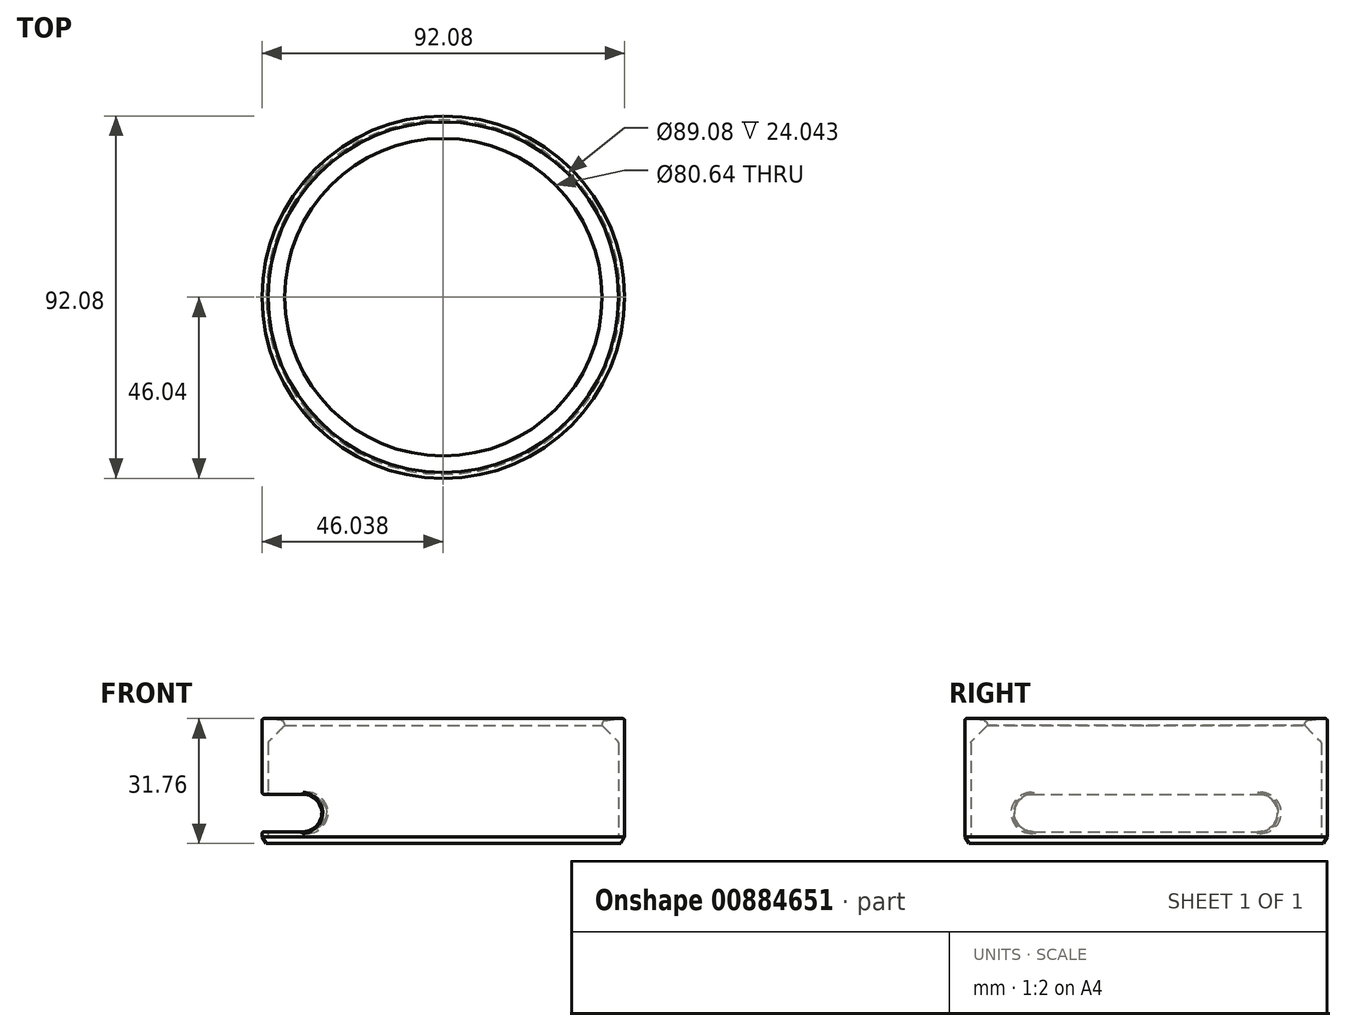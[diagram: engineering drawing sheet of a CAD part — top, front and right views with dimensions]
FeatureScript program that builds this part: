
annotation { "Feature Type Name" : "Feature", "Feature Type Description" : "" }
export const myFeature = defineFeature(function(context is Context, id is Id, definition is map)
    precondition{}
    {
        {
            var Q0;
            Q0=qCreatedBy(makeId("Front.planeOp"),FACE);
            var sketch = newSketch(context, id + "F0", { "sketchPlane" : qUnion([Q0])});
            skLineSegment(sketch, "E0.bottom", {"start": v(0.75, 15.88) * mm, "end": v(-0.75, 15.88) * mm});
            skLineSegment(sketch, "E0.right", {"start": v(-0.75, 15.88) * mm, "end": v(-0.75, -15.88) * mm});
            skPoint(sketch, "E0.middle", {"position": v(0, 0) * mm});
            skLineSegment(sketch, "E1.bottom", {"start": v(-0.75, -15.88) * mm, "end": v(45.29, -15.88) * mm});
            skLineSegment(sketch, "E1.top", {"start": v(0.75, -14.37) * mm, "end": v(45.29, -14.37) * mm});
            skLineSegment(sketch, "E1.right", {"start": v(45.29, -15.87) * mm, "end": v(45.29, -14.37) * mm});
            skLineSegment(sketch, "E2", {"start": v(0.75, 15.88) * mm, "end": v(4.97, 15.24) * mm});
            skLineSegment(sketch, "E3", {"start": v(4.97, 14.1) * mm, "end": v(0.75, 9.87) * mm});
            skLineSegment(sketch, "E4.trimOffspring", {"start": v(0.75, 9.88) * mm, "end": v(0.75, -14.38) * mm});
            skLineSegment(sketch, "E5", {"start": v(0.75, 15.88) * mm, "end": v(0.75, 9.88) * mm, "construction": true});
            skLineSegment(sketch, "E6", {"start": v(4.97, 14.1) * mm, "end": v(4.97, 15.24) * mm});
            skPoint(sketch, "E7.orphan", {"position": v(0.75, -15.88) * mm});
            skLineSegment(sketch, "E8", {"start": v(4.97, 14.66) * mm, "end": v(0.75, 14.66) * mm, "construction": true});
            skSolve(sketch);
        }
        {
            var Q0;
            Q0=makeQuery(id+"F0.imprint","IMPRINT",FACE,{"disambiguationData":[TD([[makeQuery(id+"F0.imprint","IMPRINT",EDGE,{"derivedFrom":sQuery(id+"F0.wireOp",EDGE,"E0.bottom")}),1.0]])]});
            var Q1;
            Q1=sQuery(id+"F0.wireOp",EDGE,"E1.right");
            revolve(context, id + "F1", {"surfaceOperationType" : NewSurfaceOperationType.NEW, "entities" : qUnion([Q0]), "axis" : qUnion([Q1]), "revolveType" : RevolveType.FULL});
        }
        {
            var Q0;
            Q0=qCreatedBy(makeId("Right.planeOp"),FACE);
            var sketch = newSketch(context, id + "F2", { "sketchPlane" : qUnion([Q0])});
            skLineSegment(sketch, "E9.bottom", {"start": v(28.57, -12.88) * mm, "end": v(-28.57, -12.88) * mm});
            skLineSegment(sketch, "E9.top", {"start": v(28.8, -3.35) * mm, "end": v(-28.8, -3.35) * mm});
            skPoint(sketch, "E9.middle", {"position": v(0, 0) * mm});
            skArc(sketch, "E10", {"start": v(28.57, -12.88) * mm, "mid": v(33.45, -8.22) * mm, "end": v(28.8, -3.35) * mm});
            skArc(sketch, "E11.MirrorC", {"start": v(-28.57, -12.88) * mm, "mid": v(-33.45, -8.22) * mm, "end": v(-28.8, -3.35) * mm});
            skPoint(sketch, "E12", {"position": v(33.45, -8.22) * mm});
            skPoint(sketch, "E13", {"position": v(-33.45, -8.22) * mm});
            skLineSegment(sketch, "E14.0", {"start": v(46.04, -15.88) * mm, "end": v(-46.04, -15.88) * mm, "construction": true});
            skSolve(sketch);
        }
        {
            var Q0;
            Q0 = qSketchRegion(id + "F2", true);
            extrude(context, id + "F3", {"entities" : qUnion([Q0]), "operationType" : NewBodyOperationType.REMOVE, "depth" : 50 * mm, "offsetDistance" : 25 * mm, "hasSecondDirection" : true, "secondDirectionOppositeDirection" : true, "secondDirectionDepth" : 25 * mm});
        }
        {
            var Q0;
            Q0=makeQuery(id+"F3.boolean.opBoolean","INTERSECT",EDGE,{"derivedFrom":[makeQuery(id+"F1.opRevolve","SWEPT_FACE",FACE,{"disambiguationData":[OSD([sQuery(id+"F0.wireOp",EDGE,"E0.right")])]}),makeQuery(id+"F3.opExtrude","SWEPT_FACE",FACE,{"disambiguationData":[OSD([sQuery(id+"F2.wireOp",EDGE,"E9.top")])]})]});
            var Q1;
            Q1=makeQuery(id+"F3.boolean.opBoolean","INTERSECT",EDGE,{"derivedFrom":[makeQuery(id+"F1.opRevolve","SWEPT_FACE",FACE,{"disambiguationData":[OSD([sQuery(id+"F0.wireOp",EDGE,"E0.right")])]}),makeQuery(id+"F3.opExtrude","SWEPT_FACE",FACE,{"disambiguationData":[OSD([sQuery(id+"F2.wireOp",EDGE,"E10")])]})]});
            var Q2;
            Q2=makeQuery(id+"F3.boolean.opBoolean","INTERSECT",EDGE,{"derivedFrom":[makeQuery(id+"F1.opRevolve","SWEPT_FACE",FACE,{"disambiguationData":[OSD([sQuery(id+"F0.wireOp",EDGE,"E0.right")])]}),makeQuery(id+"F3.opExtrude","SWEPT_FACE",FACE,{"disambiguationData":[OSD([sQuery(id+"F2.wireOp",EDGE,"E11.MirrorC")])]})]});
            var Q3;
            Q3=makeQuery(id+"F1.opRevolve","SWEPT_EDGE",EDGE,{"disambiguationData":[OSD([sQuery(id+"F0.wireOp",EDGE,"E0.bottom"),sQuery(id+"F0.wireOp",EDGE,"E0.right")])]});
            var Q4;
            Q4=makeQuery(id+"F3.boolean.opBoolean","INTERSECT",EDGE,{"derivedFrom":[makeQuery(id+"F1.opRevolve","SWEPT_FACE",FACE,{"disambiguationData":[OSD([sQuery(id+"F0.wireOp",EDGE,"E4.trimOffspring")])]}),makeQuery(id+"F3.opExtrude","SWEPT_FACE",FACE,{"disambiguationData":[OSD([sQuery(id+"F2.wireOp",EDGE,"E9.bottom")])]})]});
            var Q5;
            Q5=makeQuery(id+"F3.boolean.opBoolean","INTERSECT",EDGE,{"derivedFrom":[makeQuery(id+"F1.opRevolve","SWEPT_FACE",FACE,{"disambiguationData":[OSD([sQuery(id+"F0.wireOp",EDGE,"E4.trimOffspring")])]}),makeQuery(id+"F3.opExtrude","SWEPT_FACE",FACE,{"disambiguationData":[OSD([sQuery(id+"F2.wireOp",EDGE,"E9.top")])]})]});
            var Q6;
            Q6=makeQuery(id+"F3.boolean.opBoolean","INTERSECT",EDGE,{"derivedFrom":[makeQuery(id+"F1.opRevolve","SWEPT_FACE",FACE,{"disambiguationData":[OSD([sQuery(id+"F0.wireOp",EDGE,"E4.trimOffspring")])]}),makeQuery(id+"F3.opExtrude","SWEPT_FACE",FACE,{"disambiguationData":[OSD([sQuery(id+"F2.wireOp",EDGE,"E10")])]})]});
            var Q7;
            Q7=makeQuery(id+"F3.boolean.opBoolean","INTERSECT",EDGE,{"derivedFrom":[makeQuery(id+"F1.opRevolve","SWEPT_FACE",FACE,{"disambiguationData":[OSD([sQuery(id+"F0.wireOp",EDGE,"E4.trimOffspring")])]}),makeQuery(id+"F3.opExtrude","SWEPT_FACE",FACE,{"disambiguationData":[OSD([sQuery(id+"F2.wireOp",EDGE,"E11.MirrorC")])]})]});
            var Q8;
            Q8=makeQuery(id+"F1.opRevolve","SWEPT_EDGE",EDGE,{"disambiguationData":[OSD([sQuery(id+"F0.wireOp",EDGE,"E3"),sQuery(id+"F0.wireOp",EDGE,"E4.trimOffspring")])]});
            var Q9;
            Q9=makeQuery(id+"F3.boolean.opBoolean","INTERSECT",EDGE,{"derivedFrom":[makeQuery(id+"F1.opRevolve","SWEPT_FACE",FACE,{"disambiguationData":[OSD([sQuery(id+"F0.wireOp",EDGE,"E0.right")])]}),makeQuery(id+"F3.opExtrude","SWEPT_FACE",FACE,{"disambiguationData":[OSD([sQuery(id+"F2.wireOp",EDGE,"E9.bottom")])]})]});
            fillet(context, id + "F4", {"entities" : qUnion([Q0, Q1, Q2, Q3, Q4, Q5, Q6, Q7, Q8, Q9]), "radius" : 0.5 * mm, "tangentPropagation" : true, "allowEdgeOverflow" : false});
        }
        {
            var Q0;
            Q0=makeQuery(id+"F1.opRevolve","SWEPT_EDGE",EDGE,{"disambiguationData":[OSD([sQuery(id+"F0.wireOp",EDGE,"E2"),sQuery(id+"F0.wireOp",EDGE,"E6")])]});
            fillet(context, id + "F5", {"entities" : qUnion([Q0]), "radius" : 1 * mm, "tangentPropagation" : true, "allowEdgeOverflow" : false});
        }
        {
            var Q0;
            Q0=makeQuery(id+"F1.opRevolve","SWEPT_EDGE",EDGE,{"disambiguationData":[OSD([sQuery(id+"F0.wireOp",EDGE,"E0.right"),sQuery(id+"F0.wireOp",EDGE,"E1.bottom")])]});
            chamfer(context, id + "F6", {"entities" : qUnion([Q0]), "chamferType" : ChamferType.OFFSET_ANGLE, "width" : 1 * mm, "oppositeDirection" : false, "angle" : 60 * degree, "tangentPropagation" : true});
        }
    });
